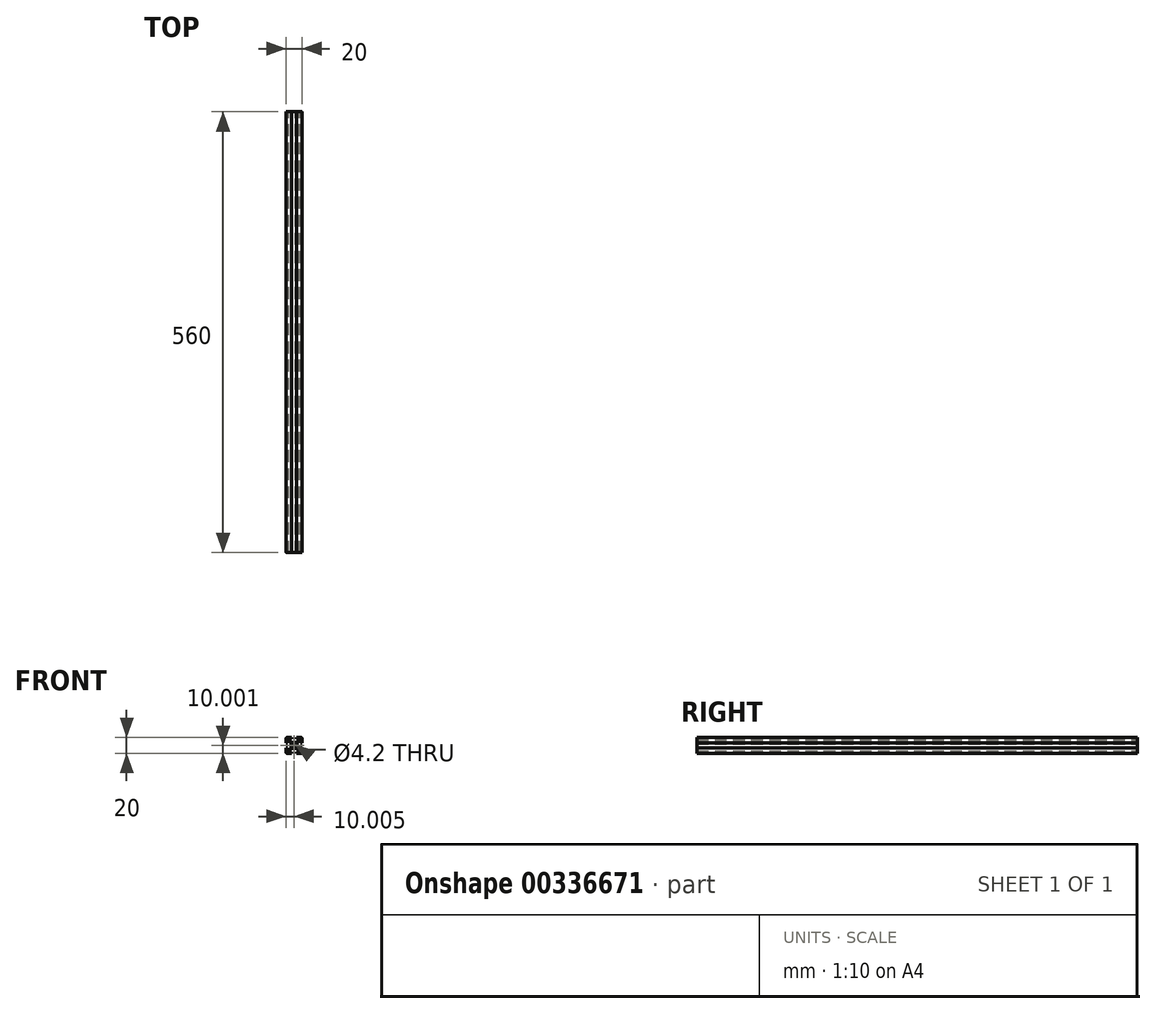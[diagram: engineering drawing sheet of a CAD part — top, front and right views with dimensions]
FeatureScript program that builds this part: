
annotation { "Feature Type Name" : "Feature", "Feature Type Description" : "" }
export const myFeature = defineFeature(function(context is Context, id is Id, definition is map)
    precondition{}
    {
        {
            var Q0;
            Q0=qCreatedBy(makeId("Front.planeOp"),FACE);
            var sketch = newSketch(context, id + "F0", { "sketchPlane" : qUnion([Q0])});
            skCircle(sketch, "E0", {"center": v(-0.06, -0.16) * mm, "radius": 2.1 * mm});
            skLineSegment(sketch, "E1.bottom", {"start": v(8.94, 9.84) * mm, "end": v(2.94, 9.84) * mm});
            skLineSegment(sketch, "E1.top", {"start": v(8.94, -10.16) * mm, "end": v(2.94, -10.16) * mm});
            skLineSegment(sketch, "E1.left", {"start": v(9.94, 8.84) * mm, "end": v(9.94, 2.84) * mm});
            skLineSegment(sketch, "E1.right", {"start": v(-10.06, 8.84) * mm, "end": v(-10.06, 2.84) * mm});
            skLineSegment(sketch, "E2.bottom", {"start": v(2.88, 3.84) * mm, "end": v(-3, 3.84) * mm});
            skLineSegment(sketch, "E2.top", {"start": v(2.88, -4.16) * mm, "end": v(-3, -4.16) * mm});
            skLineSegment(sketch, "E2.left", {"start": v(3.94, 2.78) * mm, "end": v(3.94, -3.1) * mm});
            skLineSegment(sketch, "E2.right", {"start": v(-4.06, 2.78) * mm, "end": v(-4.06, -3.1) * mm});
            skLineSegment(sketch, "E3.bottom", {"start": v(6.88, 7.84) * mm, "end": v(2.94, 7.84) * mm});
            skLineSegment(sketch, "E3.top", {"start": v(6.88, -8.16) * mm, "end": v(2.94, -8.16) * mm});
            skLineSegment(sketch, "E3.left", {"start": v(7.94, 6.78) * mm, "end": v(7.94, 2.84) * mm});
            skLineSegment(sketch, "E3.right", {"start": v(-8.06, 6.78) * mm, "end": v(-8.06, 2.84) * mm});
            skLineSegment(sketch, "E4", {"start": v(-3.06, -10.16) * mm, "end": v(-3.06, -8.16) * mm});
            skLineSegment(sketch, "E5.MirrorCS", {"start": v(2.94, -10.16) * mm, "end": v(2.94, -8.16) * mm});
            skLineSegment(sketch, "E6.MirrorCS", {"start": v(-3.06, 9.84) * mm, "end": v(-3.06, 7.84) * mm});
            skLineSegment(sketch, "E7.MirrorCS", {"start": v(2.94, 9.84) * mm, "end": v(2.94, 7.84) * mm});
            skLineSegment(sketch, "E8", {"start": v(-10.06, 2.84) * mm, "end": v(-8.06, 2.84) * mm});
            skLineSegment(sketch, "E9.MirrorCS", {"start": v(-10.06, -3.16) * mm, "end": v(-8.06, -3.16) * mm});
            skLineSegment(sketch, "E10", {"start": v(7.94, 2.84) * mm, "end": v(9.94, 2.84) * mm});
            skLineSegment(sketch, "E11.MirrorCS", {"start": v(7.94, -3.16) * mm, "end": v(9.94, -3.16) * mm});
            skPoint(sketch, "E12", {"position": v(-8.06, -7.1) * mm});
            skPoint(sketch, "E13", {"position": v(6.88, 7.84) * mm});
            skPoint(sketch, "E14", {"position": v(-4.06, -3.1) * mm});
            skPoint(sketch, "E15", {"position": v(2.88, 3.84) * mm});
            skLineSegment(sketch, "E16", {"start": v(-8.06, -7.1) * mm, "end": v(-4.06, -3.1) * mm});
            skLineSegment(sketch, "E17", {"start": v(2.88, 3.84) * mm, "end": v(6.88, 7.84) * mm});
            skLineSegment(sketch, "E18.MirrorCS", {"start": v(-7, -8.16) * mm, "end": v(-3, -4.16) * mm});
            skLineSegment(sketch, "E19.1.0", {"start": v(6.88, -8.16) * mm, "end": v(2.88, -4.16) * mm});
            skLineSegment(sketch, "E19.2.0", {"start": v(7.94, 6.78) * mm, "end": v(3.94, 2.78) * mm});
            skLineSegment(sketch, "E19.3.0", {"start": v(-7, 7.84) * mm, "end": v(-3, 3.84) * mm});
            skLineSegment(sketch, "E20.1.0", {"start": v(7.94, -7.1) * mm, "end": v(3.94, -3.1) * mm});
            skLineSegment(sketch, "E20.2.0", {"start": v(6.88, 7.84) * mm, "end": v(2.88, 3.84) * mm});
            skLineSegment(sketch, "E20.3.0", {"start": v(-8.06, 6.78) * mm, "end": v(-4.06, 2.78) * mm});
            skLineSegment(sketch, "E21.trimOffspring", {"start": v(-3.06, 7.84) * mm, "end": v(-7, 7.84) * mm});
            skLineSegment(sketch, "E22.trimOffspring", {"start": v(-3.06, 9.84) * mm, "end": v(-9.06, 9.84) * mm});
            skLineSegment(sketch, "E23.trimOffspring", {"start": v(7.94, -3.16) * mm, "end": v(7.94, -7.1) * mm});
            skLineSegment(sketch, "E24.trimOffspring", {"start": v(9.94, -3.16) * mm, "end": v(9.94, -9.16) * mm});
            skLineSegment(sketch, "E25.trimOffspring", {"start": v(-3.06, -10.16) * mm, "end": v(-9.06, -10.16) * mm});
            skLineSegment(sketch, "E26.trimOffspring", {"start": v(-3.06, -8.16) * mm, "end": v(-7, -8.16) * mm});
            skLineSegment(sketch, "E27.trimOffspring", {"start": v(-10.06, -3.16) * mm, "end": v(-10.06, -9.16) * mm});
            skLineSegment(sketch, "E28.trimOffspring", {"start": v(-8.06, -3.16) * mm, "end": v(-8.06, -7.1) * mm});
            skArc(sketch, "E29.filletArc", {"start": v(-10.06, -9.16) * mm, "mid": v(-9.76, -9.87) * mm, "end": v(-9.06, -10.16) * mm});
            skArc(sketch, "E30.filletArc", {"start": v(8.94, -10.16) * mm, "mid": v(9.65, -9.87) * mm, "end": v(9.94, -9.16) * mm});
            skArc(sketch, "E31.filletArc", {"start": v(9.94, 8.84) * mm, "mid": v(9.65, 9.55) * mm, "end": v(8.94, 9.84) * mm});
            skArc(sketch, "E32.filletArc", {"start": v(-9.06, 9.84) * mm, "mid": v(-9.76, 9.55) * mm, "end": v(-10.06, 8.84) * mm});
            skSolve(sketch);
        }
        {
            var Q0;
            Q0=makeQuery(id+"F0.imprint","IMPRINT",FACE,{"disambiguationData":[TD([[makeQuery(id+"F0.imprint","IMPRINT",EDGE,{"derivedFrom":sQuery(id+"F0.wireOp",EDGE,"E0")}),-1.0]])]});
            extrude(context, id + "F1", {"entities" : qUnion([Q0]), "depth" : 560 * mm});
        }
    });
